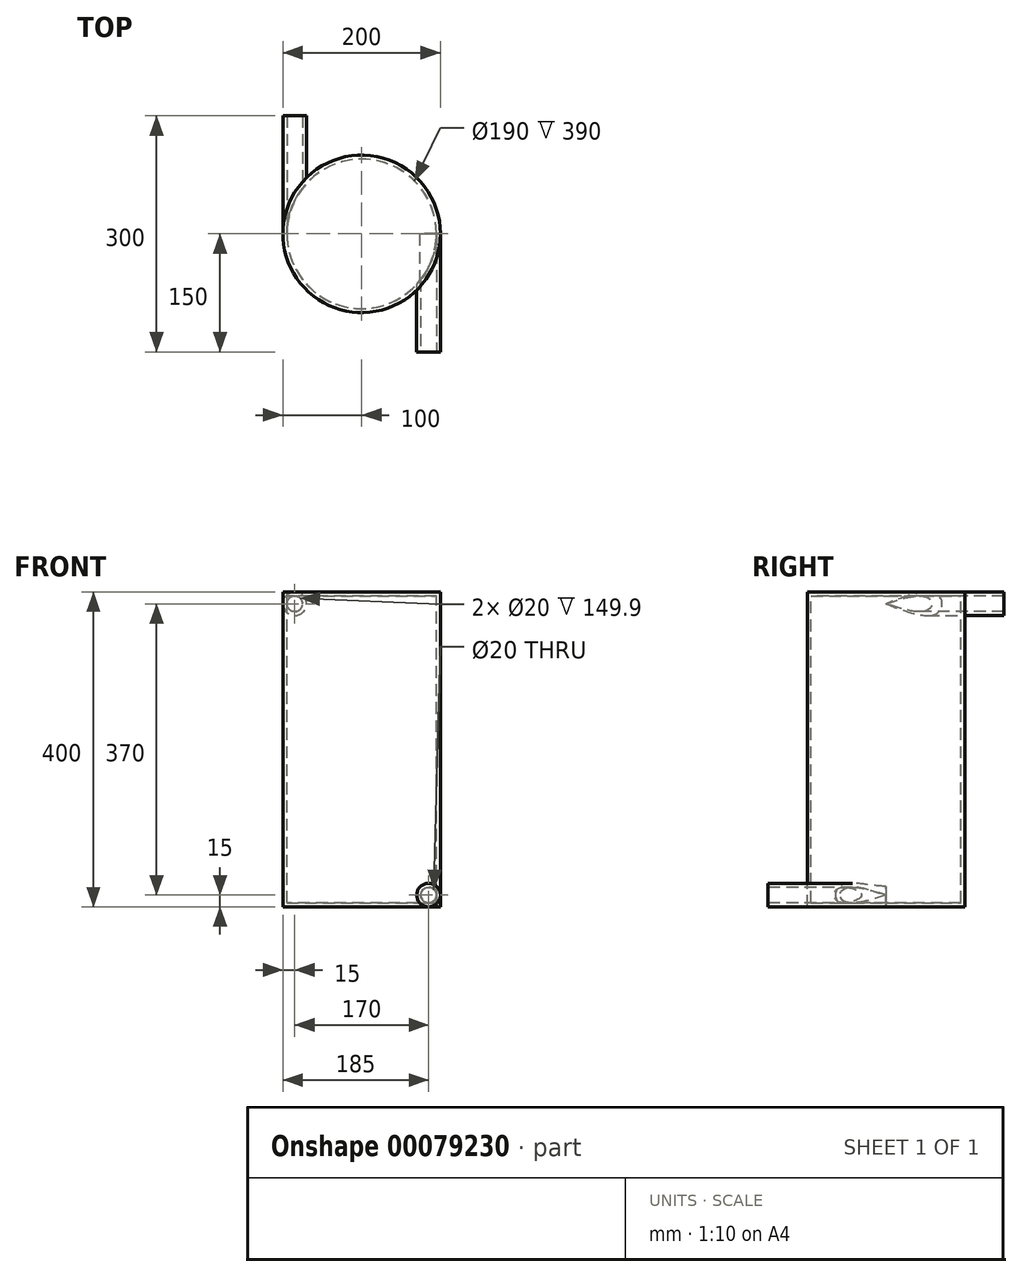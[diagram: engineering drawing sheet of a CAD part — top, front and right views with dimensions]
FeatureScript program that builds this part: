
annotation { "Feature Type Name" : "Feature", "Feature Type Description" : "" }
export const myFeature = defineFeature(function(context is Context, id is Id, definition is map)
    precondition{}
    {
        {
            var Q0;
            Q0=qCreatedBy(makeId("Top.planeOp"),FACE);
            cPlane(context, id + "F0", {"entities" : qUnion([Q0]), "cplaneType" : CPlaneType.OFFSET, "offset" : 200 * mm, "width" : 152.4 * mm, "height" : 152.4 * mm});
        }
        {
            var Q0;
            Q0=qCreatedBy(id+"F0.planeOp",FACE);
            var sketch = newSketch(context, id + "F1", { "sketchPlane" : qUnion([Q0])});
            skCircle(sketch, "E0", {"center": v(0, 0) * mm, "radius": 100 * mm});
            skCircle(sketch, "E1", {"center": v(0, 0) * mm, "radius": 95 * mm});
            skSolve(sketch);
        }
        {
            var Q0;
            Q0=makeQuery(id+"F1.imprint","IMPRINT",FACE,{"disambiguationData":[TD([[makeQuery(id+"F1.imprint","IMPRINT",EDGE,{"derivedFrom":sQuery(id+"F1.wireOp",EDGE,"E0")}),1.0]])]});
            extrude(context, id + "F2", {"entities" : qUnion([Q0]), "oppositeDirection" : true, "depth" : 400 * mm});
        }
        {
            var Q0;
            Q0=qCreatedBy(id+"F0.planeOp",FACE);
            var sketch = newSketch(context, id + "F3", { "sketchPlane" : qUnion([Q0])});
            skCircle(sketch, "E2", {"center": v(0, 0) * mm, "radius": 100 * mm});
            skSolve(sketch);
        }
        {
            var Q0;
            Q0=makeQuery(id+"F3.imprint","IMPRINT",FACE,{"disambiguationData":[TD([[makeQuery(id+"F3.imprint","IMPRINT",EDGE,{"derivedFrom":sQuery(id+"F3.wireOp",EDGE,"E2")}),1.0]])]});
            extrude(context, id + "F4", {"entities" : qUnion([Q0]), "operationType" : NewBodyOperationType.ADD, "oppositeDirection" : true, "depth" : 5 * mm});
        }
        {
            var Q0;
            Q0=qCreatedBy(makeId("Top.planeOp"),FACE);
            cPlane(context, id + "F5", {"entities" : qUnion([Q0]), "cplaneType" : CPlaneType.OFFSET, "offset" : 200 * mm, "oppositeDirection" : true, "width" : 150 * mm, "height" : 150 * mm});
        }
        {
            var Q0;
            Q0=qCreatedBy(id+"F5.planeOp",FACE);
            var sketch = newSketch(context, id + "F6", { "sketchPlane" : qUnion([Q0])});
            skCircle(sketch, "E3", {"center": v(0, 0) * mm, "radius": 100 * mm});
            skSolve(sketch);
        }
        {
            var Q0;
            Q0=makeQuery(id+"F6.imprint","IMPRINT",FACE,{"disambiguationData":[TD([[makeQuery(id+"F6.imprint","IMPRINT",EDGE,{"derivedFrom":sQuery(id+"F6.wireOp",EDGE,"E3")}),1.0]])]});
            extrude(context, id + "F7", {"entities" : qUnion([Q0]), "operationType" : NewBodyOperationType.ADD, "depth" : 5 * mm});
        }
        {
            var Q0;
            Q0=qCreatedBy(makeId("Front.planeOp"),FACE);
            var sketch = newSketch(context, id + "F8", { "sketchPlane" : qUnion([Q0])});
            skCircle(sketch, "E4", {"center": v(-85, 185) * mm, "radius": 10 * mm});
            skSolve(sketch);
        }
        {
            var Q0;
            Q0=sQuery(id+"F8.wireOp",VERTEX,"E4.center");
            var Q1;
            Q1=makeQuery(id+"F2.opExtrude","SWEPT_BODY",BODY,{"disambiguationData":[OSD([sQuery(id+"F1.wireOp",EDGE,"E0"),sQuery(id+"F1.wireOp",EDGE,"E1")])]});
            hole(context, id + "F9", {"style" : HoleStyle.SIMPLE, "endStyle" : HoleEndStyle.THROUGH, "holeDiameter" : 20 * mm, "locations" : qUnion([Q0]), "scope" : qUnion([Q1]), "isTappedThrough" : true});
        }
        {
            var Q0;
            Q0=qCreatedBy(makeId("Front.planeOp"),FACE);
            var sketch = newSketch(context, id + "F10", { "sketchPlane" : qUnion([Q0])});
            skCircle(sketch, "E5", {"center": v(85, -185) * mm, "radius": 10 * mm});
            skSolve(sketch);
        }
        {
            var Q0;
            Q0=sQuery(id+"F10.wireOp",VERTEX,"E5.center");
            var Q1;
            Q1=makeQuery(id+"F2.opExtrude","SWEPT_BODY",BODY,{"disambiguationData":[OSD([sQuery(id+"F1.wireOp",EDGE,"E0"),sQuery(id+"F1.wireOp",EDGE,"E1")])]});
            hole(context, id + "F11", {"style" : HoleStyle.SIMPLE, "endStyle" : HoleEndStyle.THROUGH, "oppositeDirection" : true, "holeDiameter" : 20 * mm, "locations" : qUnion([Q0]), "scope" : qUnion([Q1]), "isTappedThrough" : true});
        }
        {
            var Q0;
            Q0=qCreatedBy(makeId("Front.planeOp"),FACE);
            cPlane(context, id + "F12", {"entities" : qUnion([Q0]), "cplaneType" : CPlaneType.OFFSET, "offset" : 150 * mm, "width" : 150 * mm, "height" : 150 * mm});
        }
        {
            var Q0;
            Q0=qCreatedBy(makeId("Front.planeOp"),FACE);
            cPlane(context, id + "F13", {"entities" : qUnion([Q0]), "cplaneType" : CPlaneType.OFFSET, "offset" : 150 * mm, "oppositeDirection" : true, "width" : 150 * mm, "height" : 150 * mm});
        }
        {
            var Q0;
            Q0=qCreatedBy(id+"F13.planeOp",FACE);
            var sketch = newSketch(context, id + "F14", { "sketchPlane" : qUnion([Q0])});
            skCircle(sketch, "E6", {"center": v(-85, 185) * mm, "radius": 15 * mm});
            skCircle(sketch, "E7", {"center": v(-85, 185) * mm, "radius": 10 * mm});
            skSolve(sketch);
        }
        {
            var Q0;
            Q0=makeQuery(id+"F14.imprint","IMPRINT",FACE,{"disambiguationData":[TD([[makeQuery(id+"F14.imprint","IMPRINT",EDGE,{"derivedFrom":sQuery(id+"F14.wireOp",EDGE,"E6")}),1.0]])]});
            extrude(context, id + "F15", {"entities" : qUnion([Q0]), "operationType" : NewBodyOperationType.ADD, "depth" : 150 * mm});
        }
        {
            var Q0;
            Q0=qCreatedBy(id+"F12.planeOp",FACE);
            var sketch = newSketch(context, id + "F16", { "sketchPlane" : qUnion([Q0])});
            skCircle(sketch, "E8", {"center": v(85, -185) * mm, "radius": 15 * mm});
            skCircle(sketch, "E9", {"center": v(85, -185) * mm, "radius": 10 * mm});
            skSolve(sketch);
        }
        {
            var Q0;
            Q0=makeQuery(id+"F16.imprint","IMPRINT",FACE,{"disambiguationData":[TD([[makeQuery(id+"F16.imprint","IMPRINT",EDGE,{"derivedFrom":sQuery(id+"F16.wireOp",EDGE,"E8")}),1.0]])]});
            extrude(context, id + "F17", {"entities" : qUnion([Q0]), "oppositeDirection" : true, "depth" : 150 * mm});
        }
        {
            var Q0;
            Q0=qCreatedBy(makeId("Top.planeOp"),FACE);
            cPlane(context, id + "F18", {"entities" : qUnion([Q0]), "cplaneType" : CPlaneType.OFFSET, "offset" : 195 * mm, "width" : 150 * mm, "height" : 150 * mm});
        }
        {
            var Q0;
            Q0=qCreatedBy(makeId("Top.planeOp"),FACE);
            cPlane(context, id + "F19", {"entities" : qUnion([Q0]), "cplaneType" : CPlaneType.OFFSET, "offset" : 195 * mm, "oppositeDirection" : true, "width" : 150 * mm, "height" : 150 * mm});
        }
        {
            var Q0;
            Q0=qCreatedBy(id+"F18.planeOp",FACE);
            var sketch = newSketch(context, id + "F20", { "sketchPlane" : qUnion([Q0])});
            skCircle(sketch, "E10", {"center": v(0, 0) * mm, "radius": 95 * mm});
            skSolve(sketch);
        }
        {
            var Q0;
            Q0=qCreatedBy(id+"F19.planeOp",FACE);
            var sketch = newSketch(context, id + "F21", { "sketchPlane" : qUnion([Q0])});
            skCircle(sketch, "E11", {"center": v(0, 0) * mm, "radius": 95 * mm});
            skSolve(sketch);
        }
        {
            var Q0;
            Q0=makeQuery(id+"F21.imprint","IMPRINT",FACE,{"disambiguationData":[TD([[makeQuery(id+"F21.imprint","IMPRINT",EDGE,{"derivedFrom":sQuery(id+"F21.wireOp",EDGE,"E11")}),1.0]])]});
            extrude(context, id + "F22", {"entities" : qUnion([Q0]), "depth" : 40 * mm});
        }
        {
            var Q0;
            Q0=makeQuery(id+"F20.imprint","IMPRINT",FACE,{"disambiguationData":[TD([[makeQuery(id+"F20.imprint","IMPRINT",EDGE,{"derivedFrom":sQuery(id+"F20.wireOp",EDGE,"E10")}),1.0]])]});
            extrude(context, id + "F23", {"entities" : qUnion([Q0]), "oppositeDirection" : true, "depth" : 50 * mm});
        }
        {
            var Q0;
            Q0=makeQuery(id+"F22.opExtrude","SWEPT_BODY",BODY,{"disambiguationData":[OSD([sQuery(id+"F21.wireOp",EDGE,"E11")])]});
            var Q1;
            Q1=makeQuery(id+"F17.opExtrude","SWEPT_BODY",BODY,{"disambiguationData":[OSD([sQuery(id+"F16.wireOp",EDGE,"E8"),sQuery(id+"F16.wireOp",EDGE,"E9")])]});
            booleanBodies(context, id + "F24", {"operationType" : BooleanOperationType.SUBTRACTION, "tools" : qUnion([Q0]), "targets" : qUnion([Q1])});
        }
        {
            var Q0;
            Q0=makeQuery(id+"F23.opExtrude","SWEPT_BODY",BODY,{"disambiguationData":[OSD([sQuery(id+"F20.wireOp",EDGE,"E10")])]});
            var Q1;
            Q1=makeQuery(id+"F2.opExtrude","SWEPT_BODY",BODY,{"disambiguationData":[OSD([sQuery(id+"F1.wireOp",EDGE,"E0"),sQuery(id+"F1.wireOp",EDGE,"E1")])]});
            booleanBodies(context, id + "F25", {"operationType" : BooleanOperationType.SUBTRACTION, "tools" : qUnion([Q0]), "targets" : qUnion([Q1])});
        }
        {
            var Q0;
            Q0=qCreatedBy(makeId("Front.planeOp"),FACE);
            cPlane(context, id + "F26", {"entities" : qUnion([Q0]), "cplaneType" : CPlaneType.OFFSET, "offset" : 150 * mm, "width" : 150 * mm, "height" : 150 * mm});
        }
        {
            var Q0;
            Q0=qCreatedBy(id+"F26.planeOp",FACE);
            var sketch = newSketch(context, id + "F27", { "sketchPlane" : qUnion([Q0])});
            skCircle(sketch, "E12", {"center": v(85, -185) * mm, "radius": 10 * mm});
            skSolve(sketch);
        }
        {
            var Q0;
            Q0=makeQuery(id+"F27.imprint","IMPRINT",FACE,{"disambiguationData":[TD([[makeQuery(id+"F27.imprint","IMPRINT",EDGE,{"derivedFrom":sQuery(id+"F27.wireOp",EDGE,"E12")}),1.0]])]});
            var Q1;
            Q1=sQuery(id+"F27.wireOp",EDGE,"E12");
            extrude(context, id + "F28", {"entities" : qUnion([Q0]), "operationType" : NewBodyOperationType.ADD, "surfaceEntities" : qUnion([Q1]), "oppositeDirection" : true, "depth" : 0.1 * mm});
        }
        {
            var Q0;
            Q0=qCreatedBy(makeId("Front.planeOp"),FACE);
            cPlane(context, id + "F29", {"entities" : qUnion([Q0]), "cplaneType" : CPlaneType.OFFSET, "offset" : 150 * mm, "oppositeDirection" : true, "width" : 150 * mm, "height" : 150 * mm});
        }
        {
            var Q0;
            Q0=qCreatedBy(id+"F29.planeOp",FACE);
            var sketch = newSketch(context, id + "F30", { "sketchPlane" : qUnion([Q0])});
            skCircle(sketch, "E13", {"center": v(-85, 185) * mm, "radius": 10 * mm});
            skSolve(sketch);
        }
        {
            var Q0;
            Q0=makeQuery(id+"F30.imprint","IMPRINT",FACE,{"disambiguationData":[TD([[makeQuery(id+"F30.imprint","IMPRINT",EDGE,{"derivedFrom":sQuery(id+"F30.wireOp",EDGE,"E13")}),1.0]])]});
            extrude(context, id + "F31", {"entities" : qUnion([Q0]), "operationType" : NewBodyOperationType.ADD, "depth" : 0.1 * mm});
        }
    });
